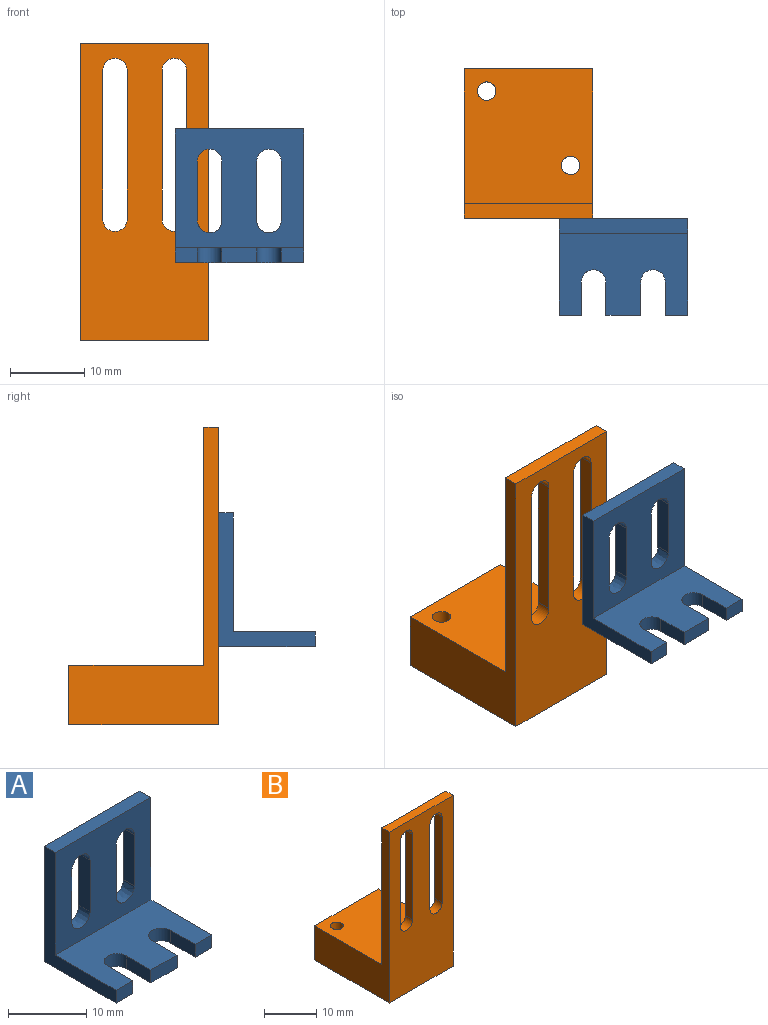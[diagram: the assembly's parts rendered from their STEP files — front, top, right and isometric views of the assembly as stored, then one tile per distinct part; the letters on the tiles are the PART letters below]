
ASSEMBLY  parts=2 mates=1
PART A: 24 faces, bbox 17.3x13x18 mm
  f0: plane 17.3x16mm, normal (0,-1,0), area 206.9mm2, adj f2,f12,f13,f15,f16,f17,f18,f19
  f1: plane 18x17.3mm, normal (0,1,0), area 241.5mm2, adj f2,f12,f14,f15,f16,f17,f18,f19
  f2: plane 18x13mm, normal (-1,0,0), area 58mm2, adj f0,f1,f3,f13,f14,f15
  f3: plane 3x2mm, normal (0,-1,0), area 6mm2, adj f2,f4,f13,f14
  f4: plane 4.45x2mm, normal (1,0,0), area 8.9mm2, adj f3,f5,f13,f14
  f5: cylinder r=1.65mm len=3.3mm, axis (0,0,-1), area 10.4mm2, adj f4,f6,f13,f14
  f6: plane 4.45x2mm, normal (-1,0,0), area 8.9mm2, adj f5,f7,f13,f14
  f7: plane 4.7x2mm, normal (0,-1,0), area 9.4mm2, adj f6,f8,f13,f14
  f8: plane 4.46x2mm, normal (1,0,0), area 8.9mm2, adj f7,f9,f13,f14
  f9: cylinder r=1.65mm len=3.3mm, axis (0,0,-1), area 10.3mm2, adj f8,f10,f13,f14
  f10: plane 4.45x2mm, normal (-1,0,0), area 8.9mm2, adj f9,f11,f13,f14
  f11: plane 3x2mm, normal (0,-1,0), area 6mm2, adj f10,f12,f13,f14
  f12: plane 18x13mm, normal (1,0,0), area 58mm2, adj f0,f1,f11,f13,f14,f15
  f13: plane 17.3x11mm, normal (0,0,1), area 152.4mm2, adj f0,f2,f3,f4,f5,f6,f7,f8
  f14: plane 17.3x13mm, normal (0,0,-1), area 187mm2, adj f1,f2,f3,f4,f5,f6,f7,f8
  f15: plane 17.3x2mm, normal (0,0,1), area 34.6mm2, adj f0,f1,f2,f12
  f16: plane 8x2mm, normal (1,0,0), area 16mm2, adj f0,f1,f17,f19
  f17: extruded ~3.3x2mm, area 10.4mm2, adj f0,f1,f16,f18
  f18: plane 8x2mm, normal (-1,0,0), area 16mm2, adj f0,f1,f17,f19
  f19: cylinder r=1.65mm len=3.3mm, axis (0,-1,0), area 10.4mm2, adj f0,f1,f16,f18
  f20: extruded ~3.3x2mm, area 10.4mm2, adj f0,f1,f21,f23
  f21: plane 8x2mm, normal (-1,0,0), area 16mm2, adj f0,f1,f20,f22
  f22: cylinder r=1.65mm len=3.3mm, axis (0,-1,0), area 10.4mm2, adj f0,f1,f21,f23
  f23: plane 8x2mm, normal (1,0,0), area 16mm2, adj f0,f1,f20,f22
PART B: 18 faces, bbox 17.3x20.2x40 mm
  f0: plane 40x17.3mm, normal (0,-1,0), area 542.9mm2, adj f2,f3,f4,f5,f6,f7,f8,f9
  f1: plane 32x17.3mm, normal (0,1,0), area 404.5mm2, adj f2,f3,f4,f5,f6,f7,f8,f9
  f2: plane 40x20.16mm, normal (-1,0,0), area 225.3mm2, adj f0,f1,f4,f13,f14,f15
  f3: plane 40x20.16mm, normal (1,0,0), area 225.3mm2, adj f0,f1,f4,f13,f14,f15
  f4: plane 17.3x2mm, normal (0,0,1), area 34.6mm2, adj f0,f1,f2,f3
  f5: plane 20x2mm, normal (1,0,0), area 40mm2, adj f0,f1,f6,f8
  f6: cylinder r=1.65mm len=3.3mm, axis (0,-1,0), area 10.4mm2, adj f0,f1,f5,f7
  f7: plane 20x2mm, normal (-1,0,0), area 40mm2, adj f0,f1,f6,f8
  f8: cylinder r=1.65mm len=3.3mm, axis (0,-1,0), area 10.4mm2, adj f0,f1,f5,f7
  f9: cylinder r=1.65mm len=3.3mm, axis (0,-1,0), area 10.4mm2, adj f0,f1,f10,f12
  f10: plane 20x2mm, normal (-1,0,0), area 40mm2, adj f0,f1,f9,f11
  f11: cylinder r=1.65mm len=3.3mm, axis (0,-1,0), area 10.4mm2, adj f0,f1,f10,f12
  f12: plane 20x2mm, normal (1,0,0), area 40mm2, adj f0,f1,f9,f11
  f13: plane 17.3x8mm, normal (0,1,0), area 138.4mm2, adj f2,f3,f14,f15
  f14: plane 20.16x17.3mm, normal (0,0,-1), area 339mm2, adj f0,f2,f3,f13,f16,f17
  f15: plane 18.16x17.3mm, normal (0,0,1), area 304.4mm2, adj f1,f2,f3,f13,f16,f17
  f16: cylinder r=1.25mm len=8mm, axis (0,0,1), area 62.8mm2, adj f14,f15
  f17: cylinder r=1.25mm len=8mm, axis (0,0,1), area 62.8mm2, adj f14,f15
PLACE A t=(-3.93,-10.2,2.12)mm
PLACE B t=(-16.67,-8.2,-0.36)mm
MATE planar B.f0 <-> A.f1  axis (0,-1,0) through (-10.16,4.92,9.89)mm
